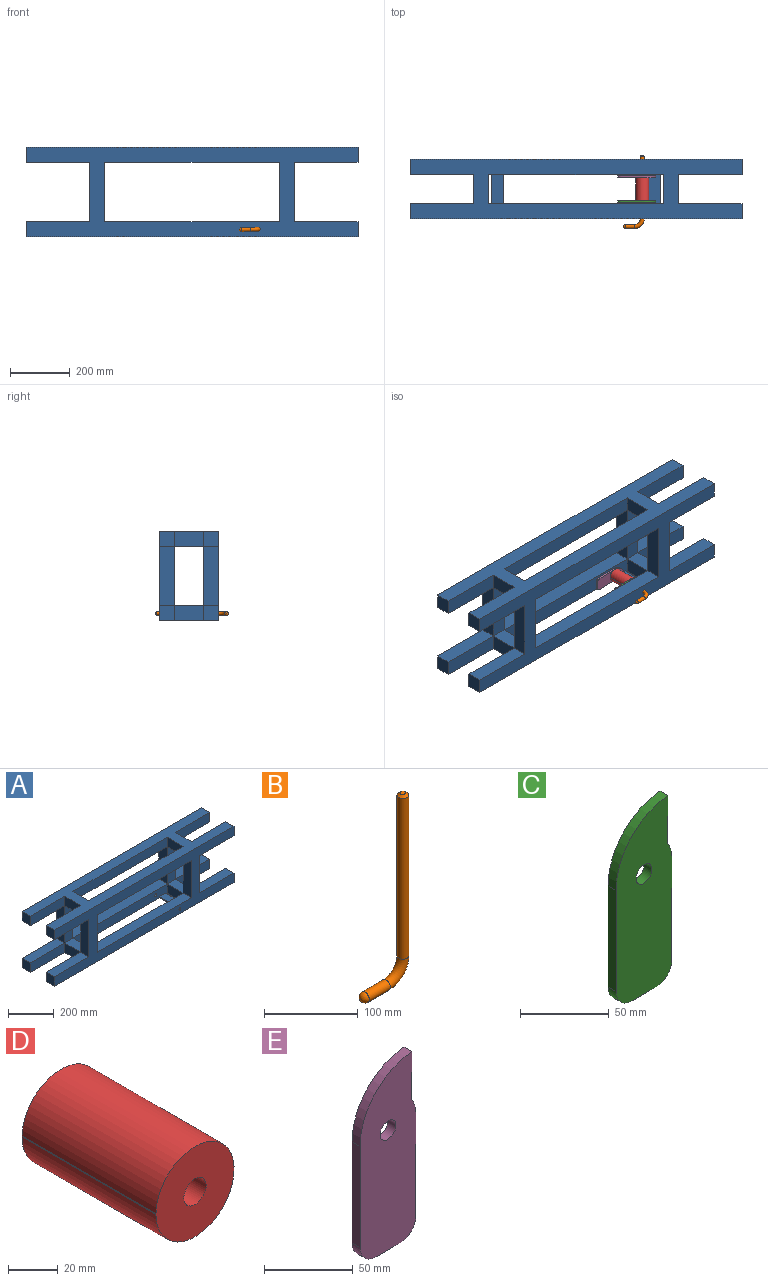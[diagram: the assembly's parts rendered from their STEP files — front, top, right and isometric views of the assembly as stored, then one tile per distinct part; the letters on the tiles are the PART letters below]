
ASSEMBLY  parts=5 mates=9
PART A: 68 faces, bbox 1114.4x200x301.6 mm
  f0: plane 1114.43x250.5mm, normal (0,1,0), area 71176mm2, adj f27,f29,f30,f31,f34,f36,f37,f38
  f1: plane 584.2x50.8mm, normal (0,-1,0), area 29066.8mm2, adj f12,f22,f31,f37,f51,f60,f61,f62
  f2: plane 214.31x50.8mm, normal (0,-1,0), area 10887.1mm2, adj f12,f13,f14,f38
  f3: plane 200.03x50.8mm, normal (0,-1,0), area 10161.3mm2, adj f15,f21,f34,f36
  f4: plane 584.2x50.8mm, normal (0,-1,0), area 29677.4mm2, adj f18,f20,f28,f33
  f5: plane 214.31x50.8mm, normal (0,-1,0), area 10887.1mm2, adj f16,f17,f18,f35
  f6: plane 200.03x50.8mm, normal (0,-1,0), area 10161.3mm2, adj f9,f19,f27,f29
  f7: plane 214.31x50.8mm, normal (0,-1,0), area 10887.1mm2, adj f8,f18,f23,f26
  f8: plane 214.31x50.8mm, normal (0,0,-1), area 10887.1mm2, adj f7,f9,f23,f25
  f9: plane 200.03x50.8mm, normal (-1,0,0), area 10161.3mm2, adj f6,f8,f10,f25
  f10: plane 214.31x50.8mm, normal (0,0,1), area 10887.1mm2, adj f9,f11,f24,f25
  f11: plane 50.8x50.8mm, normal (-1,0,0), area 2580.6mm2, adj f10,f12,f24,f25
  f12: plane 1114.43x149.23mm, normal (0,0,-1), area 70362.8mm2, adj f1,f2,f11,f13,f24,f25,f30,f31
  f13: plane 50.8x50.8mm, normal (1,0,0), area 2580.6mm2, adj f2,f12,f14,f25
  f14: plane 214.31x50.8mm, normal (0,0,1), area 10887.1mm2, adj f2,f13,f15,f25
  f15: plane 200.03x50.8mm, normal (1,0,0), area 10161.3mm2, adj f3,f14,f16,f25
  f16: plane 214.31x50.8mm, normal (0,0,-1), area 10887.1mm2, adj f5,f15,f17,f25
  f17: plane 50.8x50.8mm, normal (1,0,0), area 2580.6mm2, adj f5,f16,f18,f25
  f18: plane 1114.43x200.03mm, normal (0,0,1), area 123225.6mm2, adj f4,f5,f7,f17,f23,f25,f26,f28
  f19: plane 200.03x50.8mm, normal (1,0,0), area 10161.3mm2, adj f6,f20,f22,f25
  f20: plane 584.2x50.8mm, normal (0,0,-1), area 29677.4mm2, adj f4,f19,f21,f25
  f21: plane 200.03x50.8mm, normal (-1,0,0), area 10161.3mm2, adj f3,f20,f22,f25
  f22: plane 584.2x50.8mm, normal (0,0,1), area 29677.4mm2, adj f1,f19,f21,f25
  f23: plane 50.8x50.8mm, normal (-1,0,0), area 2580.6mm2, adj f7,f8,f18,f25
  f24: plane 214.31x50.8mm, normal (0,-1,0), area 10887.1mm2, adj f10,f11,f12,f30
  f25: plane 1114.43x301.63mm, normal (0,1,0), area 133421.4mm2, adj f8,f9,f10,f11,f12,f13,f14,f15
  f26: plane 98.43x50.8mm, normal (-1,0,0), area 5000mm2, adj f7,f18,f27,f42
  f27: plane 98.43x50.8mm, normal (0,0,-1), area 5000mm2, adj f0,f6,f26,f28
  f28: plane 98.43x50.8mm, normal (1,0,0), area 5000mm2, adj f4,f18,f27,f40
  f29: plane 98.43x50.8mm, normal (0,0,1), area 5000mm2, adj f0,f6,f30,f31
  f30: plane 98.43x50.8mm, normal (-1,0,0), area 5000mm2, adj f0,f12,f24,f29,f32
  f31: plane 98.43x50.8mm, normal (1,0,0), area 5000mm2, adj f0,f1,f12,f29,f32
  f32: plane 50.8x0.33mm, normal (0,-1,0), area 16.7mm2, adj f12,f30,f31,f51
  f33: plane 98.43x50.8mm, normal (-1,0,0), area 5000mm2, adj f4,f18,f34,f40
  f34: plane 98.43x50.8mm, normal (0,0,-1), area 5000mm2, adj f0,f3,f33,f35
  f35: plane 98.43x50.8mm, normal (1,0,0), area 5000mm2, adj f5,f18,f34,f41
  f36: plane 98.43x50.8mm, normal (0,0,1), area 5000mm2, adj f0,f3,f37,f38
  f37: plane 98.43x50.8mm, normal (-1,0,0), area 5000mm2, adj f0,f1,f12,f36,f39
  f38: plane 98.43x50.8mm, normal (1,0,0), area 5000mm2, adj f0,f2,f12,f36,f39
  f39: plane 50.8x0.33mm, normal (0,-1,0), area 16.7mm2, adj f12,f37,f38,f51
  f40: plane 584.2x50.8mm, normal (0,1,0), area 29677.4mm2, adj f18,f28,f33,f44
  f41: plane 214.31x50.8mm, normal (0,1,0), area 10887.1mm2, adj f18,f35,f55,f56
  f42: plane 214.31x50.8mm, normal (0,1,0), area 10887.1mm2, adj f18,f26,f46,f47
  f43: plane 199.7x50.8mm, normal (1,0,0), area 10144.6mm2, adj f0,f44,f57,f58
  f44: plane 584.2x50.8mm, normal (0,0,-1), area 29677.4mm2, adj f40,f43,f45,f58
  f45: plane 199.7x50.8mm, normal (-1,0,0), area 10144.6mm2, adj f0,f44,f57,f58
  f46: plane 50.8x50.8mm, normal (-1,0,0), area 2580.6mm2, adj f18,f42,f47,f58
  f47: plane 214.31x50.8mm, normal (0,0,-1), area 10887.1mm2, adj f42,f46,f48,f58
  f48: plane 199.7x50.8mm, normal (-1,0,0), area 10144.6mm2, adj f0,f47,f49,f58
  f49: plane 214.31x50.8mm, normal (0,0,1), area 10887.1mm2, adj f0,f48,f50,f58
  f50: plane 50.8x50.8mm, normal (-1,0,0), area 2580.6mm2, adj f0,f49,f51,f58
  f51: plane 1114.43x149.23mm, normal (0,0,-1), area 60362.8mm2, adj f0,f1,f32,f39,f50,f52,f58,f59
  f52: plane 50.8x50.8mm, normal (1,0,0), area 2580.6mm2, adj f0,f51,f53,f58
  f53: plane 214.31x50.8mm, normal (0,0,1), area 10887.1mm2, adj f0,f52,f54,f58
  f54: plane 199.7x50.8mm, normal (1,0,0), area 10144.6mm2, adj f0,f53,f55,f58
  f55: plane 214.31x50.8mm, normal (0,0,-1), area 10887.1mm2, adj f41,f54,f56,f58
  f56: plane 50.8x50.8mm, normal (1,0,0), area 2580.6mm2, adj f18,f41,f55,f58
  f57: plane 584.2x50.8mm, normal (0,0,1), area 29677.4mm2, adj f0,f43,f45,f58
  f58: plane 1114.43x301.3mm, normal (0,-1,0), area 133388.1mm2, adj f18,f43,f44,f45,f46,f47,f48,f49
  f59: plane 38.1x0.33mm, normal (0,-1,0), area 12.5mm2, adj f12,f51,f60,f61
  f60: plane 98.43x6.35mm, normal (1,0,0), area 625mm2, adj f0,f1,f12,f59,f62
  f61: plane 98.43x6.35mm, normal (-1,0,0), area 625mm2, adj f0,f1,f12,f59,f62
  f62: plane 98.43x38.1mm, normal (0,0,1), area 3750mm2, adj f0,f1,f60,f61
  f63: plane 98.43x6.35mm, normal (-1,0,0), area 625mm2, adj f0,f1,f51,f65
  f64: plane 98.43x6.35mm, normal (1,0,0), area 625mm2, adj f0,f1,f51,f65
  f65: plane 98.43x38.1mm, normal (0,0,1), area 3750mm2, adj f0,f1,f63,f64
  f66: cylinder r=6.35mm len=50.8mm, axis (0,-1,0), area 2026.8mm2, adj f0,f58
  f67: cylinder r=6.35mm len=50.8mm, axis (0,-1,0), area 2026.8mm2, adj f1,f25
PART B: 6 faces, bbox 72.5x12.7x247.1 mm
  f0: plane 6.35x6.35mm, normal (0,0,1), area 31.7mm2, adj f4
  f1: cylinder r=6.35mm len=209.55mm, axis (0,0,-1), area 8360.7mm2, adj f2,f4
  f2: torus R=25.4mm, axis (0,1,0), area 1591.9mm2, adj f1,f3
  f3: cylinder r=6.35mm len=31.75mm, axis (-1,0,0), area 1266.8mm2, adj f2,f5
  f4: cone r=6.35mm half-angle=45deg, axis (0,0,-1), area 134.4mm2, adj f0,f1
  f5: sphere r=6.35mm, area 253.4mm2, adj f3
PART C: 11 faces, bbox 44.5x6.4x127 mm
  f0: plane 19.05x6.35mm, normal (0,0,-1), area 121mm2, adj f1,f7,f8,f9
  f1: cylinder r=12.7mm len=12.7mm, axis (0,1,0), area 126.7mm2, adj f0,f2,f8,f9
  f2: plane 69.85x6.35mm, normal (1,0,0), area 443.5mm2, adj f1,f3,f8,f9
  f3: cylinder r=22.23mm len=11.45mm, axis (0,1,0), area 76.4mm2, adj f2,f4,f8,f9
  f4: plane 33x6.35mm, normal (1,0,0), area 209.6mm2, adj f3,f5,f8,f9
  f5: cylinder r=44.74mm len=44.6mm, axis (0,1,0), area 424.2mm2, adj f4,f6,f8,f9
  f6: plane 69.7x6.35mm, normal (-1,0,0), area 442.6mm2, adj f5,f7,f8,f9
  f7: cylinder r=12.7mm len=12.7mm, axis (0,1,0), area 126.7mm2, adj f0,f6,f8,f9
  f8: plane 127x44.45mm, normal (0,-1,0), area 4908.9mm2, adj f0,f1,f2,f3,f4,f5,f6,f7
  f9: plane 127x44.45mm, normal (0,1,0), area 4908.9mm2, adj f0,f1,f2,f3,f4,f5,f6,f7
  f10: cylinder r=6.35mm len=12.7mm, axis (0,-1,0), area 253.4mm2, adj f8,f9
PART D: 5 faces, bbox 44.5x76.2x44.5 mm
  f0: plane 44.45x44.45mm, normal (0,1,0), area 1425.1mm2, adj f2,f3,f4
  f1: plane 44.45x44.45mm, normal (0,-1,0), area 1425.1mm2, adj f2,f3,f4
  f2: cylinder r=22.23mm len=76.2mm, axis (0,-1,0), area 10608.5mm2, adj f0,f1,f3
  f3: cylinder r=44.74mm len=76.2mm, axis (0,-1,0), area 32.4mm2, adj f0,f1,f2
  f4: cylinder r=6.35mm len=76.2mm, axis (0,1,0), area 3040.2mm2, adj f0,f1
PART E: 11 faces, bbox 44.5x6.4x127 mm
  f0: plane 19.05x6.35mm, normal (0,0,-1), area 121mm2, adj f1,f7,f8,f9
  f1: cylinder r=12.7mm len=12.7mm, axis (0,1,0), area 126.7mm2, adj f0,f2,f8,f9
  f2: plane 69.85x6.35mm, normal (1,0,0), area 443.5mm2, adj f1,f3,f8,f9
  f3: cylinder r=22.23mm len=11.45mm, axis (0,1,0), area 76.4mm2, adj f2,f4,f8,f9
  f4: plane 33x6.35mm, normal (1,0,0), area 209.6mm2, adj f3,f5,f8,f9
  f5: cylinder r=44.74mm len=44.6mm, axis (0,1,0), area 424.2mm2, adj f4,f6,f8,f9
  f6: plane 69.7x6.35mm, normal (-1,0,0), area 442.6mm2, adj f5,f7,f8,f9
  f7: cylinder r=12.7mm len=12.7mm, axis (0,1,0), area 126.7mm2, adj f0,f6,f8,f9
  f8: plane 127x44.45mm, normal (0,-1,0), area 4908.9mm2, adj f0,f1,f2,f3,f4,f5,f6,f7
  f9: plane 127x44.45mm, normal (0,1,0), area 4908.9mm2, adj f0,f1,f2,f3,f4,f5,f6,f7
  f10: cylinder r=6.35mm len=12.7mm, axis (0,1,0), area 253.4mm2, adj f8,f9
PLACE A t=(-228.28,148.71,-86.41)mm fixed
PLACE B rot(axis=(-1,-0.01,-0.01),90deg) t=(551.18,161.41,-311.51)mm
PLACE C rot(axis=(0,1,0),88.5deg) t=(521.03,10.6,-312.31)mm
PLACE D rot(axis=(0,-1,0),1.9deg) t=(552.19,10.6,-341.65)mm
PLACE E rot(axis=(0,1,0),88.5deg) t=(521.03,10.6,-312.31)mm
MATE planar B.f1 <-> A.f66  axis (0,1,0) through (551.18,-51.32,-311.51)mm
MATE revolute C.f3 <-> D.f2  axis (0,1,0) through (551.18,10.6,-311.51)mm
MATE parallel B.f3 <-> C.f0  axis (-1,0,-0.03) through (525.79,-76.72,-312.18)mm
MATE planar E.f8 <-> D.f2  axis (0,-1,0) through (526.83,86.8,-312.73)mm
MATE planar C.f9 <-> D.f2  axis (0,1,0) through (526.83,10.6,-312.73)mm
MATE revolute D.f2 <-> A.f66  axis (0,-1,0) through (551.18,10.6,-311.51)mm
MATE cylindrical B.f1 <-> A.f66  axis (0,-1,0) through (551.18,53.46,-311.51)mm
MATE cylindrical E.f3 <-> D.f2  axis (0,1,0) through (551.18,93.15,-311.51)mm
MATE planar E.f6 <-> C.f6  axis (-0.03,0,1) through (515.6,89.97,-290.22)mm
